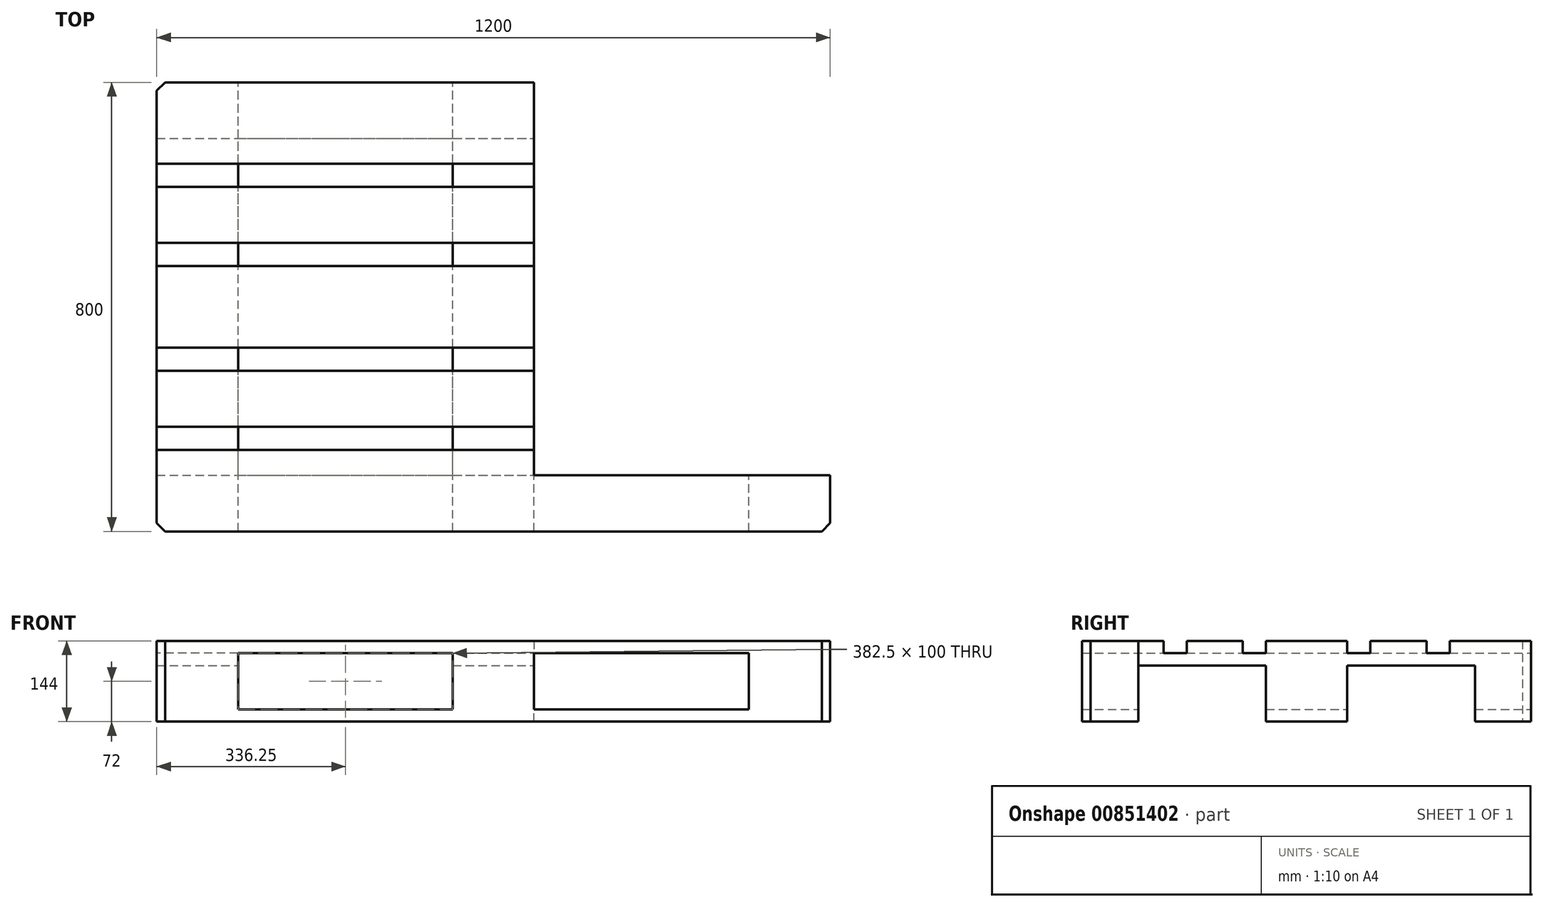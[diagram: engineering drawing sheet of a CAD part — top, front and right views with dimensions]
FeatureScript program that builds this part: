
annotation { "Feature Type Name" : "Feature", "Feature Type Description" : "" }
export const myFeature = defineFeature(function(context is Context, id is Id, definition is map)
    precondition{}
    {
        {
            var Q0;
            Q0=qCreatedBy(makeId("Top.planeOp"),FACE);
            var sketch = newSketch(context, id + "F0", { "sketchPlane" : qUnion([Q0])});
            skLineSegment(sketch, "E0.bottom", {"start": v(600, -72.5) * mm, "end": v(-600, -72.5) * mm});
            skLineSegment(sketch, "E0.top", {"start": v(600, 72.5) * mm, "end": v(-600, 72.5) * mm});
            skLineSegment(sketch, "E0.left", {"start": v(600, -72.5) * mm, "end": v(600, 72.5) * mm});
            skLineSegment(sketch, "E0.right", {"start": v(-600, -72.5) * mm, "end": v(-600, 72.5) * mm});
            skPoint(sketch, "E0.middle", {"position": v(0, 0) * mm});
            skLineSegment(sketch, "E1.bottom", {"start": v(600, -213.75) * mm, "end": v(-600, -213.75) * mm});
            skLineSegment(sketch, "E1.top", {"start": v(600, -113.75) * mm, "end": v(-600, -113.75) * mm});
            skLineSegment(sketch, "E1.left", {"start": v(600, -213.75) * mm, "end": v(600, -113.75) * mm});
            skLineSegment(sketch, "E1.right", {"start": v(-600, -213.75) * mm, "end": v(-600, -113.75) * mm});
            skPoint(sketch, "E1.middle", {"position": v(0, -163.75) * mm});
            skLineSegment(sketch, "E2.bottom", {"start": v(600, -400) * mm, "end": v(-600, -400) * mm});
            skLineSegment(sketch, "E2.top", {"start": v(600, -255) * mm, "end": v(-600, -255) * mm});
            skLineSegment(sketch, "E2.left", {"start": v(600, -400) * mm, "end": v(600, -255) * mm});
            skLineSegment(sketch, "E2.right", {"start": v(-600, -400) * mm, "end": v(-600, -255) * mm});
            skPoint(sketch, "E2.middle", {"position": v(0, -327.5) * mm});
            skLineSegment(sketch, "E3.bottom", {"start": v(-600, 213.75) * mm, "end": v(600, 213.75) * mm});
            skLineSegment(sketch, "E3.top", {"start": v(-600, 113.75) * mm, "end": v(600, 113.75) * mm});
            skLineSegment(sketch, "E3.left", {"start": v(-600, 213.75) * mm, "end": v(-600, 113.75) * mm});
            skLineSegment(sketch, "E3.right", {"start": v(600, 213.75) * mm, "end": v(600, 113.75) * mm});
            skPoint(sketch, "E3.middle", {"position": v(0, 163.75) * mm});
            skLineSegment(sketch, "E4.bottom", {"start": v(-600, 400) * mm, "end": v(600, 400) * mm});
            skLineSegment(sketch, "E4.top", {"start": v(-600, 255) * mm, "end": v(600, 255) * mm});
            skLineSegment(sketch, "E4.left", {"start": v(-600, 400) * mm, "end": v(-600, 255) * mm});
            skLineSegment(sketch, "E4.right", {"start": v(600, 400) * mm, "end": v(600, 255) * mm});
            skPoint(sketch, "E4.middle", {"position": v(0, 327.5) * mm});
            skLineSegment(sketch, "E5", {"start": v(-600, 163.75) * mm, "end": v(600, 163.75) * mm, "construction": true});
            skSolve(sketch);
        }
        {
            var Q0;
            Q0=makeQuery(id+"F0.imprint","IMPRINT",FACE,{"disambiguationData":[TD([[makeQuery(id+"F0.imprint","IMPRINT",EDGE,{"derivedFrom":sQuery(id+"F0.wireOp",EDGE,"E4.bottom")}),-1.0]])]});
            var Q1;
            Q1=makeQuery(id+"F0.imprint","IMPRINT",FACE,{"disambiguationData":[TD([[makeQuery(id+"F0.imprint","IMPRINT",EDGE,{"derivedFrom":sQuery(id+"F0.wireOp",EDGE,"E3.bottom")}),-1.0]])]});
            var Q2;
            Q2=makeQuery(id+"F0.imprint","IMPRINT",FACE,{"disambiguationData":[TD([[makeQuery(id+"F0.imprint","IMPRINT",EDGE,{"derivedFrom":sQuery(id+"F0.wireOp",EDGE,"E0.bottom")}),-1.0]])]});
            var Q3;
            Q3=makeQuery(id+"F0.imprint","IMPRINT",FACE,{"disambiguationData":[TD([[makeQuery(id+"F0.imprint","IMPRINT",EDGE,{"derivedFrom":sQuery(id+"F0.wireOp",EDGE,"E1.bottom")}),-1.0]])]});
            var Q4;
            Q4=makeQuery(id+"F0.imprint","IMPRINT",FACE,{"disambiguationData":[TD([[makeQuery(id+"F0.imprint","IMPRINT",EDGE,{"derivedFrom":sQuery(id+"F0.wireOp",EDGE,"E2.bottom")}),-1.0]])]});
            extrude(context, id + "F1", {"entities" : qUnion([Q0, Q1, Q2, Q3, Q4]), "oppositeDirection" : true, "depth" : 22 * mm, "offsetDistance" : 25 * mm});
        }
        {
            var Q0;
            Q0=makeQuery(id+"F1.opExtrude","CAP_FACE",FACE,{"disambiguationData":[OSD([sQuery(id+"F0.wireOp",EDGE,"E2.bottom"),sQuery(id+"F0.wireOp",EDGE,"E2.top"),sQuery(id+"F0.wireOp",EDGE,"E2.left"),sQuery(id+"F0.wireOp",EDGE,"E2.right")])],"isStart":false});
            var sketch = newSketch(context, id + "F2", { "sketchPlane" : qUnion([Q0])});
            skLineSegment(sketch, "E6.bottom", {"start": v(-600, 400) * mm, "end": v(-455, 400) * mm});
            skLineSegment(sketch, "E6.top", {"start": v(-600, -400) * mm, "end": v(-455, -400) * mm});
            skLineSegment(sketch, "E6.left", {"start": v(-600, 400) * mm, "end": v(-600, -400) * mm});
            skLineSegment(sketch, "E6.right", {"start": v(-455, 400) * mm, "end": v(-455, -400) * mm});
            skLineSegment(sketch, "E7.bottom", {"start": v(-72.5, 400) * mm, "end": v(72.5, 400) * mm});
            skLineSegment(sketch, "E7.top", {"start": v(-72.5, -400) * mm, "end": v(72.5, -400) * mm});
            skLineSegment(sketch, "E7.left", {"start": v(-72.5, 400) * mm, "end": v(-72.5, -400) * mm});
            skLineSegment(sketch, "E7.right", {"start": v(72.5, 400) * mm, "end": v(72.5, -400) * mm});
            skLineSegment(sketch, "E8.bottom", {"start": v(600, 400) * mm, "end": v(455, 400) * mm});
            skLineSegment(sketch, "E8.top", {"start": v(600, -400) * mm, "end": v(455, -400) * mm});
            skLineSegment(sketch, "E8.left", {"start": v(600, 400) * mm, "end": v(600, -400) * mm});
            skLineSegment(sketch, "E8.right", {"start": v(455, 400) * mm, "end": v(455, -400) * mm});
            skSolve(sketch);
        }
        {
            var Q0;
            {var subQ0=sQuery(id+"F2.wireOp",EDGE,"E6.top");Q0=makeQuery(id+"F2.imprint","IMPRINT",FACE,{"disambiguationData":[TD([[makeQuery(id+"F2.imprint","IMPRINT",EDGE,{"derivedFrom":subQ0}),1.0]])]});}
            var Q1;
            {var subQ0=sQuery(id+"F2.wireOp",EDGE,"E6.bottom");Q1=makeQuery(id+"F2.imprint","IMPRINT",FACE,{"disambiguationData":[TD([[makeQuery(id+"F2.imprint","IMPRINT",EDGE,{"derivedFrom":subQ0}),1.0]])]});}
            var Q2;
            {var subQ0=sQuery(id+"F2.wireOp",EDGE,"E7.bottom");Q2=makeQuery(id+"F2.imprint","IMPRINT",FACE,{"disambiguationData":[TD([[makeQuery(id+"F2.imprint","IMPRINT",EDGE,{"derivedFrom":subQ0}),1.0]])]});}
            var Q3;
            {var subQ0=sQuery(id+"F2.wireOp",EDGE,"E7.top");Q3=makeQuery(id+"F2.imprint","IMPRINT",FACE,{"disambiguationData":[TD([[makeQuery(id+"F2.imprint","IMPRINT",EDGE,{"derivedFrom":subQ0}),1.0]])]});}
            var Q4;
            {var subQ0=sQuery(id+"F2.wireOp",EDGE,"E8.bottom");Q4=makeQuery(id+"F2.imprint","IMPRINT",FACE,{"disambiguationData":[TD([[makeQuery(id+"F2.imprint","IMPRINT",EDGE,{"derivedFrom":subQ0}),1.0]])]});}
            var Q5;
            {var subQ0=sQuery(id+"F2.wireOp",EDGE,"E8.top");Q5=makeQuery(id+"F2.imprint","IMPRINT",FACE,{"disambiguationData":[TD([[makeQuery(id+"F2.imprint","IMPRINT",EDGE,{"derivedFrom":subQ0}),-1.0]])]});}
            extrude(context, id + "F3", {"entities" : qUnion([Q0, Q1, Q2, Q3, Q4, Q5]), "depth" : 22 * mm, "offsetDistance" : 25 * mm});
        }
        {
            var Q0;
            Q0=makeQuery(id+"F3.opExtrude","CAP_FACE",FACE,{"disambiguationData":[OSD([sQuery(id+"F2.wireOp",EDGE,"E6.bottom"),sQuery(id+"F2.wireOp",EDGE,"E6.top"),sQuery(id+"F2.wireOp",EDGE,"E6.left"),sQuery(id+"F2.wireOp",EDGE,"E6.right")])],"isStart":false});
            var sketch = newSketch(context, id + "F4", { "sketchPlane" : qUnion([Q0])});
            skLineSegment(sketch, "E9.bottom", {"start": v(-600, -400) * mm, "end": v(-455, -400) * mm});
            skLineSegment(sketch, "E9.top", {"start": v(-600, -300) * mm, "end": v(-455, -300) * mm});
            skLineSegment(sketch, "E9.left", {"start": v(-600, -400) * mm, "end": v(-600, -300) * mm});
            skLineSegment(sketch, "E9.right", {"start": v(-455, -400) * mm, "end": v(-455, -300) * mm});
            skLineSegment(sketch, "E10", {"start": v(-600, 0) * mm, "end": v(600, 0) * mm, "construction": true});
            skPoint(sketch, "E10.endSnap0", {"position": v(-600, 0) * mm});
            skLineSegment(sketch, "E11", {"start": v(0, 0) * mm, "end": v(0, 291.88) * mm, "construction": true});
            skLineSegment(sketch, "E12.MirrorCS", {"start": v(-600, 300) * mm, "end": v(-455, 300) * mm});
            skLineSegment(sketch, "E13.MirrorCS", {"start": v(-455, 400) * mm, "end": v(-455, 300) * mm});
            skLineSegment(sketch, "E14.MirrorCS", {"start": v(-600, 400) * mm, "end": v(-455, 400) * mm});
            skLineSegment(sketch, "E15.MirrorCS", {"start": v(-600, 400) * mm, "end": v(-600, 300) * mm});
            skLineSegment(sketch, "E16.bottom", {"start": v(-600, -72.5) * mm, "end": v(-455, -72.5) * mm});
            skLineSegment(sketch, "E16.top", {"start": v(-600, 72.5) * mm, "end": v(-455, 72.5) * mm});
            skLineSegment(sketch, "E16.left", {"start": v(-600, -72.5) * mm, "end": v(-600, 72.5) * mm});
            skLineSegment(sketch, "E16.right", {"start": v(-455, -72.5) * mm, "end": v(-455, 72.5) * mm});
            skPoint(sketch, "E17.MirrorP", {"position": v(600, 0) * mm});
            skLineSegment(sketch, "E18.MirrorCS", {"start": v(455, -72.5) * mm, "end": v(455, 72.5) * mm});
            skLineSegment(sketch, "E19.MirrorCS", {"start": v(600, -400) * mm, "end": v(455, -400) * mm});
            skLineSegment(sketch, "E20.MirrorCS", {"start": v(600, 400) * mm, "end": v(455, 400) * mm});
            skLineSegment(sketch, "E21.MirrorCS", {"start": v(600, -400) * mm, "end": v(600, -300) * mm});
            skLineSegment(sketch, "E22.MirrorCS", {"start": v(455, 400) * mm, "end": v(455, 300) * mm});
            skLineSegment(sketch, "E23.MirrorCS", {"start": v(600, -72.5) * mm, "end": v(455, -72.5) * mm});
            skLineSegment(sketch, "E24.MirrorCS", {"start": v(455, -400) * mm, "end": v(455, -300) * mm});
            skLineSegment(sketch, "E25.MirrorCS", {"start": v(600, 72.5) * mm, "end": v(455, 72.5) * mm});
            skLineSegment(sketch, "E26.MirrorCS", {"start": v(600, 400) * mm, "end": v(600, 300) * mm});
            skLineSegment(sketch, "E27.MirrorCS", {"start": v(600, -72.5) * mm, "end": v(600, 72.5) * mm});
            skLineSegment(sketch, "E28.MirrorCS", {"start": v(600, -300) * mm, "end": v(455, -300) * mm});
            skLineSegment(sketch, "E29.MirrorCS", {"start": v(600, 300) * mm, "end": v(455, 300) * mm});
            skPoint(sketch, "E30", {"position": v(0, 0) * mm});
            skSolve(sketch);
        }
        {
            var Q0;
            Q0=makeQuery(id+"F3.opExtrude","CAP_FACE",FACE,{"disambiguationData":[OSD([sQuery(id+"F2.wireOp",EDGE,"E7.bottom"),sQuery(id+"F2.wireOp",EDGE,"E7.top"),sQuery(id+"F2.wireOp",EDGE,"E7.left"),sQuery(id+"F2.wireOp",EDGE,"E7.right")])],"isStart":false});
            var sketch = newSketch(context, id + "F5", { "sketchPlane" : qUnion([Q0])});
            skLineSegment(sketch, "E31.bottom", {"start": v(-72.5, -400) * mm, "end": v(72.5, -400) * mm});
            skLineSegment(sketch, "E31.top", {"start": v(-72.5, -300) * mm, "end": v(72.5, -300) * mm});
            skLineSegment(sketch, "E31.left", {"start": v(-72.5, -400) * mm, "end": v(-72.5, -300) * mm});
            skLineSegment(sketch, "E31.right", {"start": v(72.5, -400) * mm, "end": v(72.5, -300) * mm});
            skLineSegment(sketch, "E32.bottom", {"start": v(-72.5, 400) * mm, "end": v(72.5, 400) * mm});
            skLineSegment(sketch, "E32.top", {"start": v(-72.5, 300) * mm, "end": v(72.5, 300) * mm});
            skLineSegment(sketch, "E32.left", {"start": v(-72.5, 400) * mm, "end": v(-72.5, 300) * mm});
            skLineSegment(sketch, "E32.right", {"start": v(72.5, 400) * mm, "end": v(72.5, 300) * mm});
            skLineSegment(sketch, "E33.bottom", {"start": v(-72.5, 72.5) * mm, "end": v(72.5, 72.5) * mm});
            skLineSegment(sketch, "E33.top", {"start": v(-72.5, -72.5) * mm, "end": v(72.5, -72.5) * mm});
            skLineSegment(sketch, "E33.left", {"start": v(-72.5, 72.5) * mm, "end": v(-72.5, -72.5) * mm});
            skLineSegment(sketch, "E33.right", {"start": v(72.5, 72.5) * mm, "end": v(72.5, -72.5) * mm});
            skPoint(sketch, "E34", {"position": v(-72.5, 0) * mm});
            skSolve(sketch);
        }
        {
            var Q0;
            Q0=makeQuery(id+"FYTJBSPpSRuX8gd_8.imprint","IMPRINT",FACE,{"disambiguationData":[TD([[makeQuery(id+"FYTJBSPpSRuX8gd_8.imprint","IMPRINT",EDGE,{"derivedFrom":sQuery(id+"FYTJBSPpSRuX8gd_8.wireOp",EDGE,"gy2sHMVN-xgZd-mj2R-ffUc-dkCIv1PvmpuS.bottom")}),1.0]])]});
            var Q1;
            Q1=makeQuery(id+"FYTJBSPpSRuX8gd_8.imprint","IMPRINT",FACE,{"disambiguationData":[TD([[makeQuery(id+"FYTJBSPpSRuX8gd_8.imprint","IMPRINT",EDGE,{"derivedFrom":sQuery(id+"FYTJBSPpSRuX8gd_8.wireOp",EDGE,"vENXevhf-lpDf-Ta8S-9Xc3-8ZelHCq2notW.bottom")}),-1.0]])]});
            var Q2;
            Q2=makeQuery(id+"FYTJBSPpSRuX8gd_8.imprint","IMPRINT",FACE,{"disambiguationData":[TD([[makeQuery(id+"FYTJBSPpSRuX8gd_8.imprint","IMPRINT",EDGE,{"derivedFrom":sQuery(id+"FYTJBSPpSRuX8gd_8.wireOp",EDGE,"zKUPhiTK-GL8t-0yBU-HGnA-DaKmiHeKaOVc.bottom")}),1.0]])]});
            var Q3;
            Q3=makeQuery(id+"FYTJBSPpSRuX8gd_8.imprint","IMPRINT",FACE,{"disambiguationData":[TD([[makeQuery(id+"FYTJBSPpSRuX8gd_8.imprint","IMPRINT",EDGE,{"derivedFrom":sQuery(id+"FYTJBSPpSRuX8gd_8.wireOp",EDGE,"ad5ac969-15a0-44eb-bdcf-7e8a1a59a2c6.1.0.7")}),1.0]])]});
            var Q4;
            Q4=makeQuery(id+"FYTJBSPpSRuX8gd_8.imprint","IMPRINT",FACE,{"disambiguationData":[TD([[makeQuery(id+"FYTJBSPpSRuX8gd_8.imprint","IMPRINT",EDGE,{"derivedFrom":sQuery(id+"FYTJBSPpSRuX8gd_8.wireOp",EDGE,"ad5ac969-15a0-44eb-bdcf-7e8a1a59a2c6.1.0.0")}),1.0]])]});
            var Q5;
            Q5=makeQuery(id+"FYTJBSPpSRuX8gd_8.imprint","IMPRINT",FACE,{"disambiguationData":[TD([[makeQuery(id+"FYTJBSPpSRuX8gd_8.imprint","IMPRINT",EDGE,{"derivedFrom":sQuery(id+"FYTJBSPpSRuX8gd_8.wireOp",EDGE,"ad5ac969-15a0-44eb-bdcf-7e8a1a59a2c6.1.0.3")}),-1.0]])]});
            var Q6;
            Q6=makeQuery(id+"FYTJBSPpSRuX8gd_8.imprint","IMPRINT",FACE,{"disambiguationData":[TD([[makeQuery(id+"FYTJBSPpSRuX8gd_8.imprint","IMPRINT",EDGE,{"derivedFrom":sQuery(id+"FYTJBSPpSRuX8gd_8.wireOp",EDGE,"ad5ac969-15a0-44eb-bdcf-7e8a1a59a2c6.2.0.3")}),-1.0]])]});
            var Q7;
            Q7=makeQuery(id+"FYTJBSPpSRuX8gd_8.imprint","IMPRINT",FACE,{"disambiguationData":[TD([[makeQuery(id+"FYTJBSPpSRuX8gd_8.imprint","IMPRINT",EDGE,{"derivedFrom":sQuery(id+"FYTJBSPpSRuX8gd_8.wireOp",EDGE,"ad5ac969-15a0-44eb-bdcf-7e8a1a59a2c6.2.0.0")}),1.0]])]});
            var Q8;
            Q8=makeQuery(id+"FYTJBSPpSRuX8gd_8.imprint","IMPRINT",FACE,{"disambiguationData":[TD([[makeQuery(id+"FYTJBSPpSRuX8gd_8.imprint","IMPRINT",EDGE,{"derivedFrom":sQuery(id+"FYTJBSPpSRuX8gd_8.wireOp",EDGE,"ad5ac969-15a0-44eb-bdcf-7e8a1a59a2c6.2.0.7")}),1.0]])]});
            var Q9;
            Q9=makeQuery(id+"F4.imprint","IMPRINT",FACE,{"disambiguationData":[TD([[makeQuery(id+"F4.imprint","IMPRINT",EDGE,{"derivedFrom":sQuery(id+"F4.wireOp",EDGE,"E9.bottom")}),1.0]])]});
            var Q10;
            Q10=makeQuery(id+"F4.imprint","IMPRINT",FACE,{"disambiguationData":[TD([[makeQuery(id+"F4.imprint","IMPRINT",EDGE,{"derivedFrom":sQuery(id+"F4.wireOp",EDGE,"E12.MirrorCS")}),1.0]])]});
            var Q11;
            Q11=makeQuery(id+"F4.imprint","IMPRINT",FACE,{"disambiguationData":[TD([[makeQuery(id+"F4.imprint","IMPRINT",EDGE,{"derivedFrom":sQuery(id+"F4.wireOp",EDGE,"E19.MirrorCS")}),-1.0]])]});
            var Q12;
            Q12=makeQuery(id+"F4.imprint","IMPRINT",FACE,{"disambiguationData":[TD([[makeQuery(id+"F4.imprint","IMPRINT",EDGE,{"derivedFrom":sQuery(id+"F4.wireOp",EDGE,"E18.MirrorCS")}),-1.0]])]});
            var Q13;
            Q13=makeQuery(id+"F4.imprint","IMPRINT",FACE,{"disambiguationData":[TD([[makeQuery(id+"F4.imprint","IMPRINT",EDGE,{"derivedFrom":sQuery(id+"F4.wireOp",EDGE,"E20.MirrorCS")}),1.0]])]});
            var Q14;
            Q14=makeQuery(id+"F4.imprint","IMPRINT",FACE,{"disambiguationData":[TD([[makeQuery(id+"F4.imprint","IMPRINT",EDGE,{"derivedFrom":sQuery(id+"F4.wireOp",EDGE,"E16.bottom")}),1.0]])]});
            var Q15;
            Q15=makeQuery(id+"F5.imprint","IMPRINT",FACE,{"disambiguationData":[TD([[makeQuery(id+"F5.imprint","IMPRINT",EDGE,{"derivedFrom":sQuery(id+"F5.wireOp",EDGE,"E33.bottom")}),-1.0]])]});
            var Q16;
            Q16=makeQuery(id+"F5.imprint","IMPRINT",FACE,{"disambiguationData":[TD([[makeQuery(id+"F5.imprint","IMPRINT",EDGE,{"derivedFrom":sQuery(id+"F5.wireOp",EDGE,"E32.bottom")}),1.0]])]});
            var Q17;
            Q17=makeQuery(id+"F5.imprint","IMPRINT",FACE,{"disambiguationData":[TD([[makeQuery(id+"F5.imprint","IMPRINT",EDGE,{"derivedFrom":sQuery(id+"F5.wireOp",EDGE,"E31.bottom")}),1.0]])]});
            extrude(context, id + "F6", {"entities" : qUnion([Q0, Q1, Q2, Q3, Q4, Q5, Q6, Q7, Q8, Q9, Q10, Q11, Q12, Q13, Q14, Q15, Q16, Q17]), "depth" : 78 * mm, "offsetDistance" : 25 * mm});
        }
        {
            var Q0;
            Q0=makeQuery(id+"F6.opExtrude","CAP_FACE",FACE,{"disambiguationData":[OSD([sQuery(id+"F4.wireOp",EDGE,"E9.bottom"),sQuery(id+"F4.wireOp",EDGE,"E9.top"),sQuery(id+"F4.wireOp",EDGE,"E9.left"),sQuery(id+"F4.wireOp",EDGE,"E9.right")])],"isStart":false});
            var sketch = newSketch(context, id + "F7", { "sketchPlane" : qUnion([Q0])});
            skLineSegment(sketch, "E35.bottom", {"start": v(-600, -400) * mm, "end": v(600, -400) * mm});
            skLineSegment(sketch, "E35.top", {"start": v(-600, -300) * mm, "end": v(600, -300) * mm});
            skLineSegment(sketch, "E35.left", {"start": v(-600, -400) * mm, "end": v(-600, -300) * mm});
            skLineSegment(sketch, "E35.right", {"start": v(600, -400) * mm, "end": v(600, -300) * mm});
            skLineSegment(sketch, "E36.bottom", {"start": v(-600, -72.5) * mm, "end": v(600, -72.5) * mm});
            skLineSegment(sketch, "E36.top", {"start": v(-600, 72.5) * mm, "end": v(600, 72.5) * mm});
            skLineSegment(sketch, "E36.left", {"start": v(-600, -72.5) * mm, "end": v(-600, 72.5) * mm});
            skLineSegment(sketch, "E36.right", {"start": v(600, -72.5) * mm, "end": v(600, 72.5) * mm});
            skLineSegment(sketch, "E37.bottom", {"start": v(-600, 300) * mm, "end": v(600, 300) * mm});
            skLineSegment(sketch, "E37.top", {"start": v(-600, 400) * mm, "end": v(600, 400) * mm});
            skLineSegment(sketch, "E37.left", {"start": v(-600, 300) * mm, "end": v(-600, 400) * mm});
            skLineSegment(sketch, "E37.right", {"start": v(600, 300) * mm, "end": v(600, 400) * mm});
            skSolve(sketch);
        }
        {
            var Q0;
            {var subQ0=sQuery(id+"F7.wireOp",EDGE,"E35.left");Q0=makeQuery(id+"F7.imprint","IMPRINT",FACE,{"disambiguationData":[TD([[makeQuery(id+"F7.imprint","IMPRINT",EDGE,{"derivedFrom":subQ0}),1.0]])]});}
            var Q1;
            {var subQ2=sQuery(id+"F7.wireOp",EDGE,"E35.right");Q1=makeQuery(id+"F7.imprint","IMPRINT",FACE,{"disambiguationData":[TD([[makeQuery(id+"F7.imprint","IMPRINT",EDGE,{"derivedFrom":subQ2}),1.0]])]});}
            var Q2;
            Q2=makeQuery(id+"F7.imprint","IMPRINT",FACE,{"disambiguationData":[TD([[makeQuery(id+"F7.imprint","IMPRINT",EDGE,{"derivedFrom":sQuery(id+"F7.wireOp",EDGE,"E36.bottom")}),1.0]])]});
            var Q3;
            Q3=makeQuery(id+"F7.imprint","IMPRINT",FACE,{"disambiguationData":[TD([[makeQuery(id+"F7.imprint","IMPRINT",EDGE,{"derivedFrom":sQuery(id+"F7.wireOp",EDGE,"E37.bottom")}),1.0]])]});
            extrude(context, id + "F8", {"entities" : qUnion([Q0, Q1, Q2, Q3]), "depth" : 22 * mm, "offsetDistance" : 25 * mm});
        }
        {
            var Q0;
            Q0=makeQuery(id+"F3.opExtrude","SWEPT_BODY",BODY,{"disambiguationData":[OSD([sQuery(id+"F2.wireOp",EDGE,"E8.bottom"),sQuery(id+"F2.wireOp",EDGE,"E8.top"),sQuery(id+"F2.wireOp",EDGE,"E8.left"),sQuery(id+"F2.wireOp",EDGE,"E8.right")])]});
            var Q1;
            Q1=makeQuery(id+"F3.opExtrude","SWEPT_BODY",BODY,{"disambiguationData":[OSD([sQuery(id+"F2.wireOp",EDGE,"E7.bottom"),sQuery(id+"F2.wireOp",EDGE,"E7.top"),sQuery(id+"F2.wireOp",EDGE,"E7.left"),sQuery(id+"F2.wireOp",EDGE,"E7.right")])]});
            var Q2;
            Q2=makeQuery(id+"F3.opExtrude","SWEPT_BODY",BODY,{"disambiguationData":[OSD([sQuery(id+"F2.wireOp",EDGE,"E6.bottom"),sQuery(id+"F2.wireOp",EDGE,"E6.top"),sQuery(id+"F2.wireOp",EDGE,"E6.left"),sQuery(id+"F2.wireOp",EDGE,"E6.right")])]});
            var Q3;
            Q3=makeQuery(id+"F1.opExtrude","SWEPT_BODY",BODY,{"disambiguationData":[OSD([sQuery(id+"F0.wireOp",EDGE,"E4.bottom"),sQuery(id+"F0.wireOp",EDGE,"E4.top"),sQuery(id+"F0.wireOp",EDGE,"E4.left"),sQuery(id+"F0.wireOp",EDGE,"E4.right")])]});
            var Q4;
            Q4=makeQuery(id+"F1.opExtrude","SWEPT_BODY",BODY,{"disambiguationData":[OSD([sQuery(id+"F0.wireOp",EDGE,"E3.bottom"),sQuery(id+"F0.wireOp",EDGE,"E3.top"),sQuery(id+"F0.wireOp",EDGE,"E3.left"),sQuery(id+"F0.wireOp",EDGE,"E3.right")])]});
            var Q5;
            Q5=makeQuery(id+"F1.opExtrude","SWEPT_BODY",BODY,{"disambiguationData":[OSD([sQuery(id+"F0.wireOp",EDGE,"E2.bottom"),sQuery(id+"F0.wireOp",EDGE,"E2.top"),sQuery(id+"F0.wireOp",EDGE,"E2.left"),sQuery(id+"F0.wireOp",EDGE,"E2.right")])]});
            var Q6;
            Q6=makeQuery(id+"F1.opExtrude","SWEPT_BODY",BODY,{"disambiguationData":[OSD([sQuery(id+"F0.wireOp",EDGE,"E1.bottom"),sQuery(id+"F0.wireOp",EDGE,"E1.top"),sQuery(id+"F0.wireOp",EDGE,"E1.left"),sQuery(id+"F0.wireOp",EDGE,"E1.right")])]});
            var Q7;
            Q7=makeQuery(id+"F1.opExtrude","SWEPT_BODY",BODY,{"disambiguationData":[OSD([sQuery(id+"F0.wireOp",EDGE,"E0.bottom"),sQuery(id+"F0.wireOp",EDGE,"E0.top"),sQuery(id+"F0.wireOp",EDGE,"E0.left"),sQuery(id+"F0.wireOp",EDGE,"E0.right")])]});
            var Q8;
            Q8=makeQuery(id+"F6.opExtrude","SWEPT_BODY",BODY,{"disambiguationData":[OSD([sQuery(id+"F4.wireOp",EDGE,"E9.bottom"),sQuery(id+"F4.wireOp",EDGE,"E9.top"),sQuery(id+"F4.wireOp",EDGE,"E9.left"),sQuery(id+"F4.wireOp",EDGE,"E9.right")])]});
            var Q9;
            Q9=makeQuery(id+"F6.opExtrude","SWEPT_BODY",BODY,{"disambiguationData":[OSD([sQuery(id+"F4.wireOp",EDGE,"E12.MirrorCS"),sQuery(id+"F4.wireOp",EDGE,"E13.MirrorCS"),sQuery(id+"F4.wireOp",EDGE,"E14.MirrorCS"),sQuery(id+"F4.wireOp",EDGE,"E15.MirrorCS")])]});
            var Q10;
            Q10=makeQuery(id+"F6.opExtrude","SWEPT_BODY",BODY,{"disambiguationData":[OSD([sQuery(id+"F4.wireOp",EDGE,"E18.MirrorCS"),sQuery(id+"F4.wireOp",EDGE,"E23.MirrorCS"),sQuery(id+"F4.wireOp",EDGE,"E25.MirrorCS"),sQuery(id+"F4.wireOp",EDGE,"E27.MirrorCS")])]});
            var Q11;
            Q11=makeQuery(id+"F6.opExtrude","SWEPT_BODY",BODY,{"disambiguationData":[OSD([sQuery(id+"F4.wireOp",EDGE,"E16.bottom"),sQuery(id+"F4.wireOp",EDGE,"E16.top"),sQuery(id+"F4.wireOp",EDGE,"E16.left"),sQuery(id+"F4.wireOp",EDGE,"E16.right")])]});
            var Q12;
            Q12=makeQuery(id+"F8.opExtrude","SWEPT_BODY",BODY,{"disambiguationData":[OSD([sQuery(id+"F7.wireOp",EDGE,"E36.bottom"),sQuery(id+"F7.wireOp",EDGE,"E36.top"),sQuery(id+"F7.wireOp",EDGE,"E36.left"),sQuery(id+"F7.wireOp",EDGE,"E36.right")])]});
            var Q13;
            Q13=makeQuery(id+"F8.opExtrude","SWEPT_BODY",BODY,{"disambiguationData":[OSD([sQuery(id+"F7.wireOp",EDGE,"E37.bottom"),sQuery(id+"F7.wireOp",EDGE,"E37.top"),sQuery(id+"F7.wireOp",EDGE,"E37.left"),sQuery(id+"F7.wireOp",EDGE,"E37.right")])]});
            var Q14;
            Q14=makeQuery(id+"F6.opExtrude","SWEPT_BODY",BODY,{"disambiguationData":[OSD([sQuery(id+"F4.wireOp",EDGE,"E20.MirrorCS"),sQuery(id+"F4.wireOp",EDGE,"E22.MirrorCS"),sQuery(id+"F4.wireOp",EDGE,"E26.MirrorCS"),sQuery(id+"F4.wireOp",EDGE,"E29.MirrorCS")])]});
            var Q15;
            Q15=makeQuery(id+"F6.opExtrude","SWEPT_BODY",BODY,{"disambiguationData":[OSD([sQuery(id+"F4.wireOp",EDGE,"E19.MirrorCS"),sQuery(id+"F4.wireOp",EDGE,"E21.MirrorCS"),sQuery(id+"F4.wireOp",EDGE,"E24.MirrorCS"),sQuery(id+"F4.wireOp",EDGE,"E28.MirrorCS")])]});
            var Q16;
            Q16=makeQuery(id+"F8.opExtrude","SWEPT_BODY",BODY,{"disambiguationData":[OSD([sQuery(id+"F7.wireOp",EDGE,"E35.bottom"),sQuery(id+"F7.wireOp",EDGE,"E35.top"),sQuery(id+"F7.wireOp",EDGE,"E35.left"),sQuery(id+"F7.wireOp",EDGE,"E35.right")])]});
            var Q17;
            Q17=makeQuery(id+"F6.opExtrude","SWEPT_BODY",BODY,{"disambiguationData":[OSD([sQuery(id+"F5.wireOp",EDGE,"E31.bottom"),sQuery(id+"F5.wireOp",EDGE,"E31.top"),sQuery(id+"F5.wireOp",EDGE,"E31.left"),sQuery(id+"F5.wireOp",EDGE,"E31.right")])]});
            var Q18;
            Q18=makeQuery(id+"F6.opExtrude","SWEPT_BODY",BODY,{"disambiguationData":[OSD([sQuery(id+"F5.wireOp",EDGE,"E33.bottom"),sQuery(id+"F5.wireOp",EDGE,"E33.top"),sQuery(id+"F5.wireOp",EDGE,"E33.left"),sQuery(id+"F5.wireOp",EDGE,"E33.right")])]});
            var Q19;
            Q19=makeQuery(id+"F6.opExtrude","SWEPT_BODY",BODY,{"disambiguationData":[OSD([sQuery(id+"F5.wireOp",EDGE,"E32.bottom"),sQuery(id+"F5.wireOp",EDGE,"E32.top"),sQuery(id+"F5.wireOp",EDGE,"E32.left"),sQuery(id+"F5.wireOp",EDGE,"E32.right")])]});
            booleanBodies(context, id + "F9", {"operationType" : BooleanOperationType.UNION, "tools" : qUnion([Q0, Q1, Q2, Q3, Q4, Q5, Q6, Q7, Q8, Q9, Q10, Q11, Q12, Q13, Q14, Q15, Q16, Q17, Q18, Q19])});
        }
        {
            var Q0;
            Q0=makeQuery(id+"F1.opExtrude","SWEPT_EDGE",EDGE,{"disambiguationData":[OSD([sQuery(id+"F0.wireOp",EDGE,"E2.bottom"),sQuery(id+"F0.wireOp",EDGE,"E2.right")])]});
            var Q1;
            Q1=makeQuery(id+"F3.opExtrude","SWEPT_EDGE",EDGE,{"disambiguationData":[OSD([sQuery(id+"F2.wireOp",EDGE,"E6.bottom"),sQuery(id+"F2.wireOp",EDGE,"E6.left")])]});
            var Q2;
            Q2=makeQuery(id+"F6.opExtrude","SWEPT_EDGE",EDGE,{"disambiguationData":[OSD([sQuery(id+"FYTJBSPpSRuX8gd_8.wireOp",EDGE,"gy2sHMVN-xgZd-mj2R-ffUc-dkCIv1PvmpuS.bottom"),sQuery(id+"FYTJBSPpSRuX8gd_8.wireOp",EDGE,"gy2sHMVN-xgZd-mj2R-ffUc-dkCIv1PvmpuS.left")])]});
            var Q3;
            Q3=makeQuery(id+"F8.opExtrude","SWEPT_EDGE",EDGE,{"disambiguationData":[OSD([sQuery(id+"FUbmOA5CFNu3vIk_17.wireOp",EDGE,"HQ4nohft-M4JY-dTNH-rdQb-ztwkA5vyvlAQ.bottom"),sQuery(id+"FUbmOA5CFNu3vIk_17.wireOp",EDGE,"HQ4nohft-M4JY-dTNH-rdQb-ztwkA5vyvlAQ.left")])]});
            var Q4;
            Q4=makeQuery(id+"F1.opExtrude","SWEPT_EDGE",EDGE,{"disambiguationData":[OSD([sQuery(id+"F0.wireOp",EDGE,"E2.bottom"),sQuery(id+"F0.wireOp",EDGE,"E2.left")])]});
            var Q5;
            Q5=makeQuery(id+"F3.opExtrude","SWEPT_EDGE",EDGE,{"disambiguationData":[OSD([sQuery(id+"F2.wireOp",EDGE,"E8.bottom"),sQuery(id+"F2.wireOp",EDGE,"E8.left")])]});
            var Q6;
            Q6=makeQuery(id+"F6.opExtrude","SWEPT_EDGE",EDGE,{"disambiguationData":[OSD([sQuery(id+"FYTJBSPpSRuX8gd_8.wireOp",EDGE,"ad5ac969-15a0-44eb-bdcf-7e8a1a59a2c6.2.0.3"),sQuery(id+"FYTJBSPpSRuX8gd_8.wireOp",EDGE,"ad5ac969-15a0-44eb-bdcf-7e8a1a59a2c6.2.0.8")])]});
            var Q7;
            Q7=makeQuery(id+"F8.opExtrude","SWEPT_EDGE",EDGE,{"disambiguationData":[OSD([sQuery(id+"FUbmOA5CFNu3vIk_17.wireOp",EDGE,"HQ4nohft-M4JY-dTNH-rdQb-ztwkA5vyvlAQ.bottom"),sQuery(id+"FUbmOA5CFNu3vIk_17.wireOp",EDGE,"HQ4nohft-M4JY-dTNH-rdQb-ztwkA5vyvlAQ.right")])]});
            var Q8;
            Q8=makeQuery(id+"F1.opExtrude","SWEPT_EDGE",EDGE,{"disambiguationData":[OSD([sQuery(id+"F0.wireOp",EDGE,"E4.bottom"),sQuery(id+"F0.wireOp",EDGE,"E4.right")])]});
            var Q9;
            Q9=makeQuery(id+"F3.opExtrude","SWEPT_EDGE",EDGE,{"disambiguationData":[OSD([sQuery(id+"F2.wireOp",EDGE,"E8.top"),sQuery(id+"F2.wireOp",EDGE,"E8.left")])]});
            var Q10;
            Q10=makeQuery(id+"F6.opExtrude","SWEPT_EDGE",EDGE,{"disambiguationData":[OSD([sQuery(id+"FYTJBSPpSRuX8gd_8.wireOp",EDGE,"ad5ac969-15a0-44eb-bdcf-7e8a1a59a2c6.2.0.7"),sQuery(id+"FYTJBSPpSRuX8gd_8.wireOp",EDGE,"ad5ac969-15a0-44eb-bdcf-7e8a1a59a2c6.2.0.9")])]});
            var Q11;
            Q11=makeQuery(id+"F8.opExtrude","SWEPT_EDGE",EDGE,{"disambiguationData":[OSD([sQuery(id+"FUbmOA5CFNu3vIk_17.wireOp",EDGE,"4kciwtxH-OBSt-f0dC-ou1O-WIhG8iqRsqLm.top"),sQuery(id+"FUbmOA5CFNu3vIk_17.wireOp",EDGE,"4kciwtxH-OBSt-f0dC-ou1O-WIhG8iqRsqLm.right")])]});
            var Q12;
            Q12=makeQuery(id+"F1.opExtrude","SWEPT_EDGE",EDGE,{"disambiguationData":[OSD([sQuery(id+"F0.wireOp",EDGE,"E4.bottom"),sQuery(id+"F0.wireOp",EDGE,"E4.left")])]});
            var Q13;
            Q13=makeQuery(id+"F3.opExtrude","SWEPT_EDGE",EDGE,{"disambiguationData":[OSD([sQuery(id+"F2.wireOp",EDGE,"E6.top"),sQuery(id+"F2.wireOp",EDGE,"E6.left")])]});
            var Q14;
            Q14=makeQuery(id+"F6.opExtrude","SWEPT_EDGE",EDGE,{"disambiguationData":[OSD([sQuery(id+"FYTJBSPpSRuX8gd_8.wireOp",EDGE,"zKUPhiTK-GL8t-0yBU-HGnA-DaKmiHeKaOVc.bottom"),sQuery(id+"FYTJBSPpSRuX8gd_8.wireOp",EDGE,"zKUPhiTK-GL8t-0yBU-HGnA-DaKmiHeKaOVc.left")])]});
            var Q15;
            Q15=makeQuery(id+"F8.opExtrude","SWEPT_EDGE",EDGE,{"disambiguationData":[OSD([sQuery(id+"FUbmOA5CFNu3vIk_17.wireOp",EDGE,"4kciwtxH-OBSt-f0dC-ou1O-WIhG8iqRsqLm.top"),sQuery(id+"FUbmOA5CFNu3vIk_17.wireOp",EDGE,"4kciwtxH-OBSt-f0dC-ou1O-WIhG8iqRsqLm.left")])]});
            chamfer(context, id + "F10", {"entities" : qUnion([Q0, Q1, Q2, Q3, Q4, Q5, Q6, Q7, Q8, Q9, Q10, Q11, Q12, Q13, Q14, Q15]), "width" : 15 * mm, "tangentPropagation" : true});
        }
        {
            var Q0;
            Q0=makeQuery(id+"F8.opExtrude","CAP_FACE",FACE,{"disambiguationData":[OSD([sQuery(id+"F7.wireOp",EDGE,"E36.bottom"),sQuery(id+"F7.wireOp",EDGE,"E36.top"),sQuery(id+"F7.wireOp",EDGE,"E36.left"),sQuery(id+"F7.wireOp",EDGE,"E36.right")])],"isStart":false});
            var sketch = newSketch(context, id + "F11", { "sketchPlane" : qUnion([Q0])});
            skLineSegment(sketch, "E38.bottom", {"start": v(672.5, 300) * mm, "end": v(72.5, 300) * mm});
            skLineSegment(sketch, "E38.top", {"start": v(672.5, -500) * mm, "end": v(72.5, -500) * mm});
            skLineSegment(sketch, "E38.left", {"start": v(672.5, 300) * mm, "end": v(672.5, -500) * mm});
            skLineSegment(sketch, "E38.right", {"start": v(72.5, 300) * mm, "end": v(72.5, -500) * mm});
            skSolve(sketch);
        }
        {
            var Q0;
            {var subQ5=makeQuery(id+"F8.opExtrude","CAP_EDGE",EDGE,{"disambiguationData":[OSD([sQuery(id+"F7.wireOp",EDGE,"E36.right")])],"isStart":false});Q0=makeQuery(id+"F11.imprint","IMPRINT",FACE,{"disambiguationData":[TD([[makeQuery(id+"F11.imprint","IMPRINT",EDGE,{"derivedFrom":subQ5}),1.0]])]});}
            var Q1;
            {var subQ1=sQuery(id+"F11.wireOp",EDGE,"E38.bottom");Q1=makeQuery(id+"F11.imprint","IMPRINT",FACE,{"disambiguationData":[TD([[makeQuery(id+"F11.imprint","IMPRINT",EDGE,{"derivedFrom":subQ1}),1.0]])]});}
            extrude(context, id + "F12", {"entities" : qUnion([Q0, Q1]), "operationType" : NewBodyOperationType.REMOVE, "oppositeDirection" : true, "depth" : 211 * mm, "offsetDistance" : 25 * mm});
        }
    });
